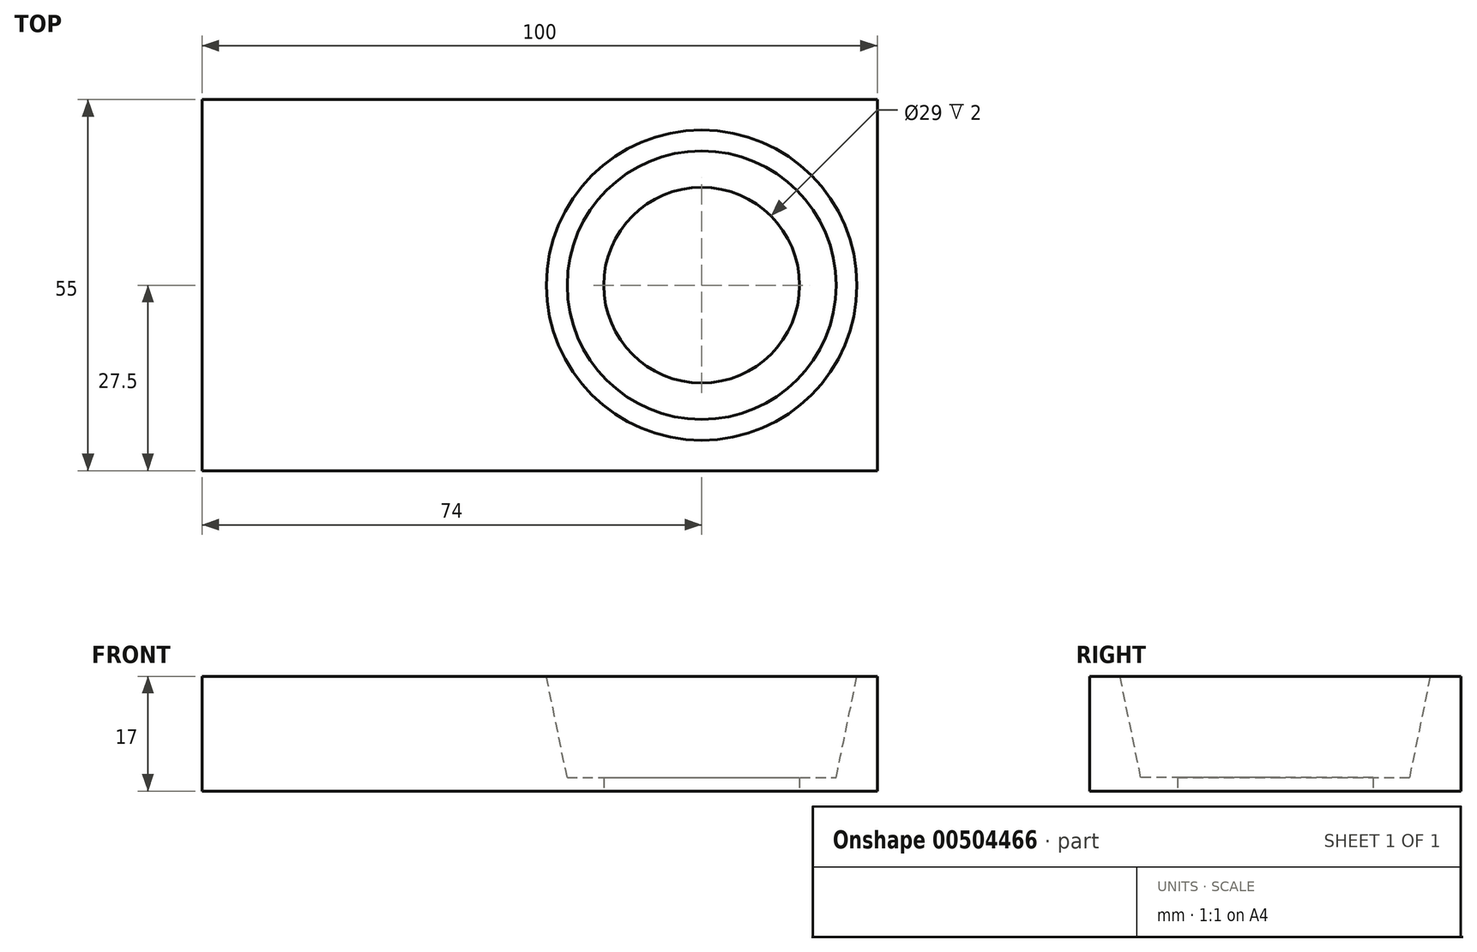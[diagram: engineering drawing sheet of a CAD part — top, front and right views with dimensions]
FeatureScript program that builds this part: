
annotation { "Feature Type Name" : "Feature", "Feature Type Description" : "" }
export const myFeature = defineFeature(function(context is Context, id is Id, definition is map)
    precondition{}
    {
        {
            var Q0;
            Q0=qCreatedBy(makeId("Top.planeOp"),FACE);
            var sketch = newSketch(context, id + "F0", { "sketchPlane" : qUnion([Q0])});
            skLineSegment(sketch, "E0.bottom", {"start": v(-50, 27.5) * mm, "end": v(50, 27.5) * mm});
            skLineSegment(sketch, "E0.top", {"start": v(-50, -27.5) * mm, "end": v(50, -27.5) * mm});
            skLineSegment(sketch, "E0.left", {"start": v(-50, 27.5) * mm, "end": v(-50, -27.5) * mm});
            skLineSegment(sketch, "E0.right", {"start": v(50, 27.5) * mm, "end": v(50, -27.5) * mm});
            skSolve(sketch);
        }
        {
            var Q0;
            Q0 = qSketchRegion(id + "F0", true);
            extrude(context, id + "F1", {"entities" : qUnion([Q0]), "depth" : 17 * mm, "offsetDistance" : 25 * mm});
        }
        {
            var Q0;
            Q0=makeQuery(id+"F1.opExtrude","CAP_FACE",FACE,{"disambiguationData":[OSD([sQuery(id+"F0.wireOp",EDGE,"E0.bottom"),sQuery(id+"F0.wireOp",EDGE,"E0.top"),sQuery(id+"F0.wireOp",EDGE,"E0.left"),sQuery(id+"F0.wireOp",EDGE,"E0.right")])],"isStart":true});
            var sketch = newSketch(context, id + "F2", { "sketchPlane" : qUnion([Q0])});
            skLineSegment(sketch, "E1", {"start": v(50, 0) * mm, "end": v(24, 0) * mm});
            skPoint(sketch, "E1.endSnap0", {"position": v(50, 0) * mm});
            skCircle(sketch, "E2", {"center": v(24, 0) * mm, "radius": 20.5 * mm});
            skCircle(sketch, "E3", {"center": v(24, 0) * mm, "radius": 19.5 * mm});
            skSolve(sketch);
        }
        {
            var Q0;
            Q0=makeQuery(id+"F1.opExtrude","CAP_FACE",FACE,{"disambiguationData":[OSD([sQuery(id+"F0.wireOp",EDGE,"E0.bottom"),sQuery(id+"F0.wireOp",EDGE,"E0.top"),sQuery(id+"F0.wireOp",EDGE,"E0.left"),sQuery(id+"F0.wireOp",EDGE,"E0.right")])],"isStart":false});
            var sketch = newSketch(context, id + "F3", { "sketchPlane" : qUnion([Q0])});
            skLineSegment(sketch, "E4", {"start": v(50, 0) * mm, "end": v(24, 0) * mm});
            skPoint(sketch, "E4.endSnap0", {"position": v(50, 0) * mm});
            skCircle(sketch, "E5", {"center": v(24, 0) * mm, "radius": 25 * mm});
            skCircle(sketch, "E6", {"center": v(24, 0) * mm, "radius": 23 * mm});
            skSolve(sketch);
        }
        {
            var Q1;
            Q1=makeQuery(id+"F3.imprint","IMPRINT",FACE,{"disambiguationData":[TD([[makeQuery(id+"F3.imprint","IMPRINT",EDGE,{"derivedFrom":sQuery(id+"F3.wireOp",EDGE,"E6")}),1.0]])]});
            var Q2;
            Q2=makeQuery(id+"F2.imprint","IMPRINT",FACE,{"disambiguationData":[TD([[makeQuery(id+"F2.imprint","IMPRINT",EDGE,{"derivedFrom":sQuery(id+"F2.wireOp",EDGE,"E3")}),1.0]])]});
            loft(context, id + "F4", {"operationType" : NewBodyOperationType.REMOVE, "sheetProfilesArray" : [{ "sheetProfileEntities" : qUnion([Q1]) }, { "sheetProfileEntities" : qUnion([Q2]) }]});
        }
        {
            var Q0;
            Q0=makeQuery(id+"F1.opExtrude","CAP_FACE",FACE,{"disambiguationData":[OSD([sQuery(id+"F0.wireOp",EDGE,"E0.bottom"),sQuery(id+"F0.wireOp",EDGE,"E0.top"),sQuery(id+"F0.wireOp",EDGE,"E0.left"),sQuery(id+"F0.wireOp",EDGE,"E0.right")])],"isStart":true});
            var sketch = newSketch(context, id + "F5", { "sketchPlane" : qUnion([Q0])});
            skLineSegment(sketch, "E7", {"start": v(50, 0) * mm, "end": v(24, 0) * mm});
            skPoint(sketch, "E7.endSnap0", {"position": v(50, 0) * mm});
            skCircle(sketch, "E8", {"center": v(24, 0) * mm, "radius": 20.5 * mm});
            skCircle(sketch, "E9", {"center": v(24, 0) * mm, "radius": 14.5 * mm});
            skSolve(sketch);
        }
        {
            var Q0;
            Q0 = qSketchRegion(id + "F5", true);
            extrude(context, id + "F6", {"entities" : qUnion([Q0]), "operationType" : NewBodyOperationType.ADD, "oppositeDirection" : true, "depth" : 2 * mm, "offsetDistance" : 25 * mm});
        }
    });
